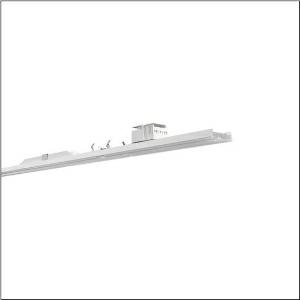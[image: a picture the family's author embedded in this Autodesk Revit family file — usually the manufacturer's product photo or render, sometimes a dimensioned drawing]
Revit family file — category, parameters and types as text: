
# Revit family: licross_r__11_recessed_ho_51tl1edn4c5r_e0e1
name_source: partatom
category: Lighting Fixtures
units: mm (PartAtom-declared; Revit-internal decimal feet)

## family parameters
Cut with Voids When Loaded = No
Host = Face
Light Source = No
Part Type = Normal
Room Calculation Point = No
Round Connector Dimension = Use Diameter
Shared = No

## types (1)
- --- (1 x LED, 12680 lm, 76.8 W, 4000K)
    Apparent Load = 77 VA
    CIE Flux Codes = 85 95 99 100 100
    Color Rendering = 80
    Color Temperature = 4000K
    Default Elevation = 1800 mm
    Description = Licross® 11 Recessed HO, luminaire insert, of sheet steel, galvanised, coil coated, white, length: 1.500mm, width: 66mm, height: 67mm, LED rated luminous flux: 12.680lm, light colour: 840, control gear: DALI 2, control gear: ECG DALI, with plug, 5-pole, with phase selection, mains connection: 220..240V, AC, 50/60Hz, halogen-free wiring, primary optical cover: cover, of PMMA, light emission: direct distribution, protection rating (complete): IP40, insulation class (complete): insulation class I (protective earthing), certification: CE, ENEC, VDE, UKCA, protection symbol: D if used in an environment without relevant dust loads with corresponding accessories, permissible ambient temperature for indoor applications: -25..+30°C, reducing of maximum allowable ambient temperature of 5°C with ceiling mounting, corresponds to IFS (International Featured Standards) requirements for safety and quality in the food industry, LABS conformity tested according to VDMA 24364:2018-05, packaging unit: 1 piece
    Height = 58 mm
    Lamp = 1 x LED
    Lamp Light Flux = 12680 lm
    Lamp Power = 76.8 W
    Lamp count = 1
    Length = 1500 mm
    Luminous efficacy = 165 lm/W
    Manufacturer = Siteco
    ModVariant = No
    Model = 51TL1EDN4C5R
    Mounting Place = Ceiling
    Mounting Type = Pendant
    Number of Poles = 1
    OnlyDefault = Yes
    Power Factor = 1
    Product Name = Licross® 11 Recessed HO
    Product group = luminaire insert
    ProductGroupID = 902
    Protection Class = Protection class I
    Protection Degree = IP 40
    RLX_Detail_Level = 1
    RlxData = <blob elided: 22657 chars, md5=f3bb28d5>
    Socket = socket
    Standby Power = 0 W
    System Light Flux = 12680 lm
    System Power = 77 W
    Type Comments = factory setting: luminous flux: 100 % | dim-lin: 254 | 435 mA
    Type Image = l_1266722.jpg
    URL = http://relux.com
    VarID = @adj_093049
    Voltage = 0 V
    Weight = 0.00 kg
    Width = 66 mm

## geometry (parser evidence)
native form markers: Blend x4, Sweep x12
no freeform markers — native parametric forms only
